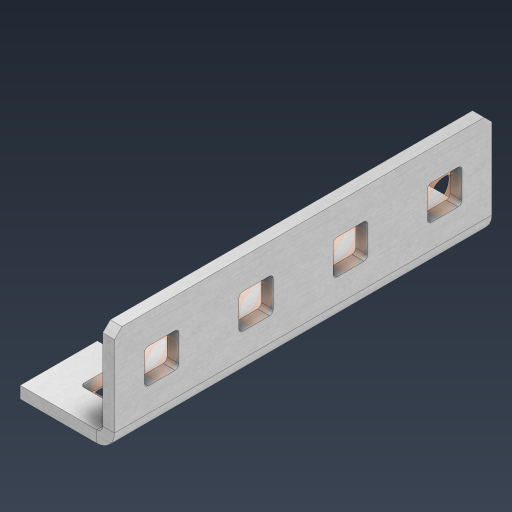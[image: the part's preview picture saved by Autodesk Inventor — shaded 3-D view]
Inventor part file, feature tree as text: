
AUTODESK INVENTOR PART (.ipt)
format: ipt  version: 2024.3 (Build 283343000, 343)  size: 461,312 bytes
history: native  units: in
note: dims shown in document units (in); Inventor stores cm internally (conversion verified against a paired STEP export)
features: other x19, sheet_metal_op x11, extrude x10, pattern_linear x2, mirror x1, chamfer x1, sketch x1
ambient origin geometry x8: Origin, YZ Plane, XZ Plane, XY Plane, X Axis, Y Axis, Z Axis, Center Point
bodies: Solid1 (feature_tree), Body (feature_tree)
feature tree (45):
  sheet_metal_op  "Flanges"
  other  "Flange Pattern Plane"
  other  "Flange Pattern Sketch"
  sheet_metal_op  "Flange Pattern"
  sheet_metal_op  "Body Pattern"
  pattern_linear  "Center Pattern"  Spacing1=2.0in  [1 undecoded]
  other  "Arc Length"
  mirror  "Notch Mirror"
  pattern_linear  "Notch Pattern"  Spacing1=0.0625in  [1 undecoded]
  chamfer  "End Chamfer"
  extrude  "Half Cut"  Depth=0.0625in
  other  "Plate1"
  sketch  "Sketch2"  dims[d0=1.0in d1=2.0in d2=0.0625in d3=0.0625in d4=0.0312in d5=0.125in d6=0.0625in d7=0.5in d8=90.0deg d9=0.0312in d10=0.25in d11=0.0625in d12=0.0625in d16=0.182in d17=0.02in d18=0.0625in d19=0.0in d20=0.25in d21=0.25in d38=1.5748in d40=0.5in d41=0.3937in d43=1.0in d46=0.172in d47=1.0in d48=0.0in d49=0.182in d50=0.02in d51=0.25in d52=0.25in d53=0.0625in d54=0.0in d55=0.172in d56=1.0in d57=0.0in d58=0.25in d60=1.5748in d62=0.5in d63=0.3937in d65=0.5in d85=0.1473in d86=0.1782in d88=0.04in d89=0.0625in d90=0.0in d91=0.04in d92=0.0491in d95=2.5in d96=0.04in d97=0.25in d98=45.0deg d99=0.25in d100=0.5in d101=0.0in d102=2.497in d106=0.182in d107=0.02in d108=0.5in d109=0.5in d110=0.0625in d111=0.0in d112=0.172in d113=0.5in d114=0.0in d117=0.5in d118=0.5in d119=0.5in]
  other  "Plate2"
  sheet_metal_op  "Bend1"
  sheet_metal_op  "Corner1"
  other  "Srf1"
  other  "Srf2"
  other  "Srf91"
  sheet_metal_op  "Body Pattern Sketch"
  other  "Srf92"
  other  "Srf786"
  other  "Srf823"
  other  "Srf824"
  other  "Srf856"
  other  "Srf857"
  other  "Srf889"
  other  "Srf890"
  other  "Srf891"
  sheet_metal_op  "Flange Stamp"
  sheet_metal_op  "Flange Circle"
  sheet_metal_op  "Body Stamp"
  sheet_metal_op  "Body Circle"
  other  "Center Stamp"
  other  "Center Circle"
  sheet_metal_op  "Notch"
  extrude  "ExtrusionSrf2"  Depth=0.0312in
  extrude  "ExtrusionSrf92"  Depth=0.5in
  extrude  "ExtrusionSrf823"  Depth=0.0625in
  extrude  "ExtrusionSrf824"  Depth=0.5in TaperAngle=90.0deg
  extrude  "ExtrusionSrf856"  Depth=0.25in
  extrude  "ExtrusionSrf857"  Depth=0.0625in
  extrude  "ExtrusionSrf889"  Depth=0.0625in
  extrude  "ExtrusionSrf890"  Depth=0.182in
  extrude  "ExtrusionSrf891"  Depth=0.02in
note: 2 required parameter values undecoded (feature->parameter linkage not recoverable at this tier; creation-order binding heuristic only, values carry confidence <= 0.55)
